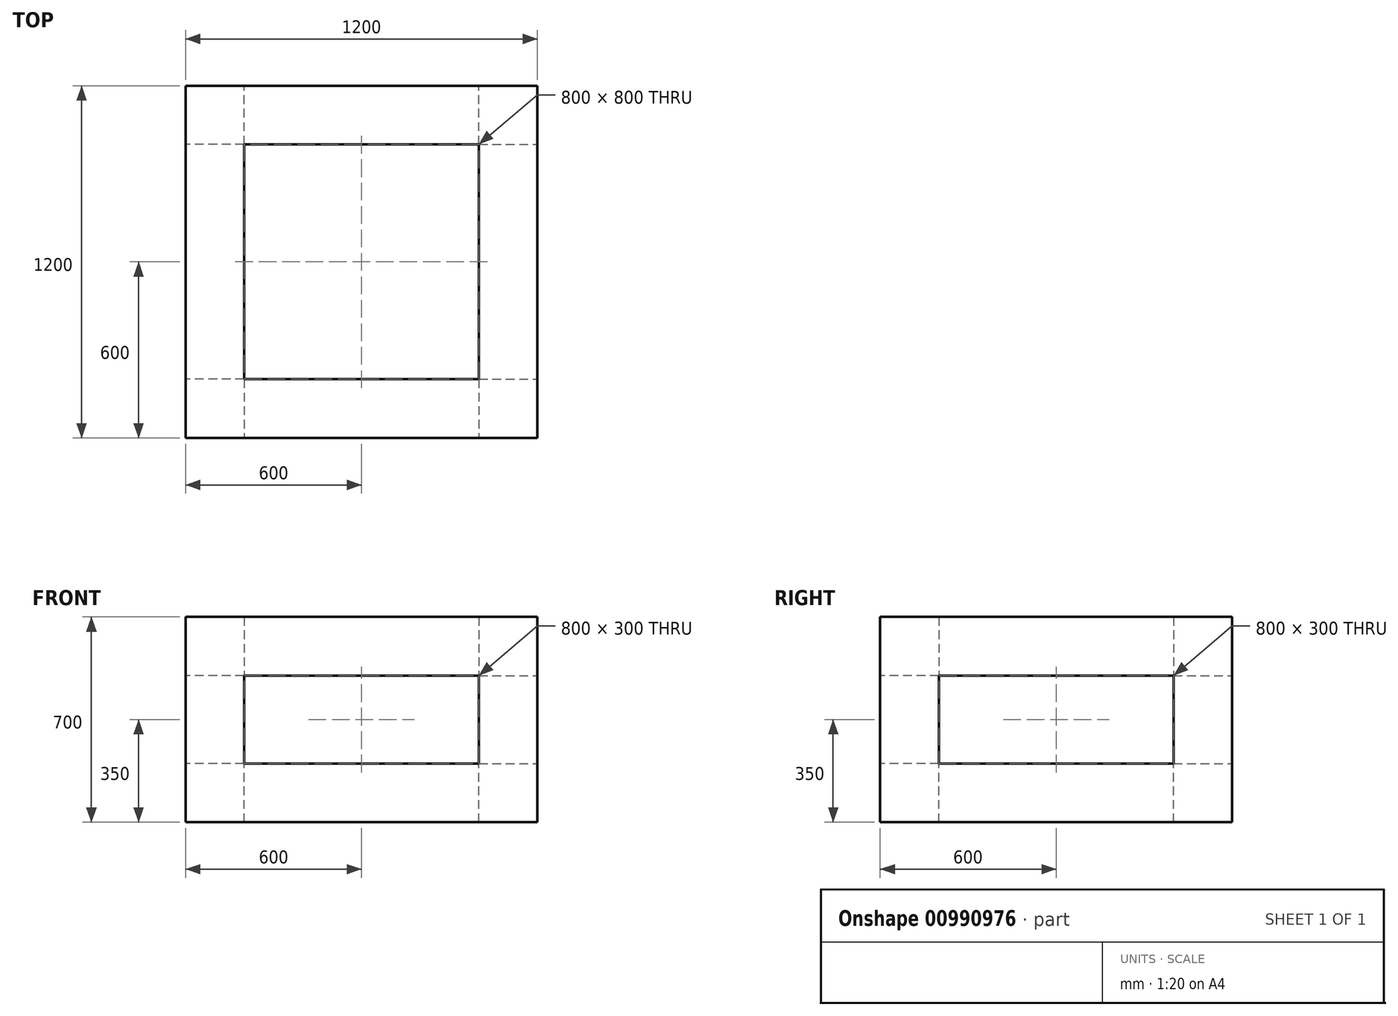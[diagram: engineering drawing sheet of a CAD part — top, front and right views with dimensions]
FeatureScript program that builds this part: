
annotation { "Feature Type Name" : "Feature", "Feature Type Description" : "" }
export const myFeature = defineFeature(function(context is Context, id is Id, definition is map)
    precondition{}
    {
        {
            var Q0;
            Q0=qCreatedBy(makeId("Top.planeOp"),FACE);
            var sketch = newSketch(context, id + "F0", { "sketchPlane" : qUnion([Q0])});
            skLineSegment(sketch, "E0.bottom", {"start": v(600, -600) * mm, "end": v(-600, -600) * mm});
            skLineSegment(sketch, "E0.top", {"start": v(600, 600) * mm, "end": v(-600, 600) * mm});
            skLineSegment(sketch, "E0.left", {"start": v(600, -600) * mm, "end": v(600, 600) * mm});
            skLineSegment(sketch, "E0.right", {"start": v(-600, -600) * mm, "end": v(-600, 600) * mm});
            skPoint(sketch, "E0.middle", {"position": v(0, 0) * mm});
            skLineSegment(sketch, "E1.bottom", {"start": v(400, -400) * mm, "end": v(-400, -400) * mm});
            skLineSegment(sketch, "E1.top", {"start": v(400, 400) * mm, "end": v(-400, 400) * mm});
            skLineSegment(sketch, "E1.left", {"start": v(400, -400) * mm, "end": v(400, 400) * mm});
            skLineSegment(sketch, "E1.right", {"start": v(-400, -400) * mm, "end": v(-400, 400) * mm});
            skLineSegment(sketch, "E2", {"start": v(-400, 400) * mm, "end": v(-600, 400) * mm});
            skLineSegment(sketch, "E3", {"start": v(-400, 400) * mm, "end": v(-400, 600) * mm});
            skLineSegment(sketch, "E4", {"start": v(400, 400) * mm, "end": v(400, 600) * mm});
            skLineSegment(sketch, "E5", {"start": v(400, 400) * mm, "end": v(600, 400) * mm});
            skLineSegment(sketch, "E6", {"start": v(-400, -400) * mm, "end": v(-600, -400) * mm});
            skLineSegment(sketch, "E7", {"start": v(-400, -400) * mm, "end": v(-400, -600) * mm});
            skLineSegment(sketch, "E8", {"start": v(400, -400) * mm, "end": v(600, -400) * mm});
            skLineSegment(sketch, "E9", {"start": v(400, -400) * mm, "end": v(400, -600) * mm});
            skSolve(sketch);
        }
        {
            var Q0;
            {var subQ4=sQuery(id+"F0.wireOp",EDGE,"E2");Q0=makeQuery(id+"F0.imprint","IMPRINT",FACE,{"disambiguationData":[TD([[makeQuery(id+"F0.imprint","IMPRINT",EDGE,{"derivedFrom":subQ4}),-1.0]])]});}
            var Q1;
            Q1=makeQuery(id+"F0.imprint","IMPRINT",FACE,{"disambiguationData":[TD([[makeQuery(id+"F0.imprint","IMPRINT",EDGE,{"derivedFrom":sQuery(id+"F0.wireOp",EDGE,"E1.top")}),-1.0]])]});
            var Q2;
            {var subQ3=sQuery(id+"F0.wireOp",EDGE,"E4");Q2=makeQuery(id+"F0.imprint","IMPRINT",FACE,{"disambiguationData":[TD([[makeQuery(id+"F0.imprint","IMPRINT",EDGE,{"derivedFrom":subQ3}),-1.0]])]});}
            var Q3;
            Q3=makeQuery(id+"F0.imprint","IMPRINT",FACE,{"disambiguationData":[TD([[makeQuery(id+"F0.imprint","IMPRINT",EDGE,{"derivedFrom":sQuery(id+"F0.wireOp",EDGE,"E1.left")}),-1.0]])]});
            var Q4;
            Q4=makeQuery(id+"F0.imprint","IMPRINT",FACE,{"disambiguationData":[TD([[makeQuery(id+"F0.imprint","IMPRINT",EDGE,{"derivedFrom":sQuery(id+"F0.wireOp",EDGE,"E1.bottom")}),-1.0]])]});
            var Q5;
            Q5=makeQuery(id+"F0.imprint","IMPRINT",FACE,{"disambiguationData":[TD([[makeQuery(id+"F0.imprint","IMPRINT",EDGE,{"derivedFrom":sQuery(id+"F0.wireOp",EDGE,"E1.right")}),1.0]])]});
            var Q6;
            {var subQ4=sQuery(id+"F0.wireOp",EDGE,"E6");Q6=makeQuery(id+"F0.imprint","IMPRINT",FACE,{"disambiguationData":[TD([[makeQuery(id+"F0.imprint","IMPRINT",EDGE,{"derivedFrom":subQ4}),1.0]])]});}
            var Q7;
            Q7=makeQuery(id+"F0.imprint","IMPRINT",FACE,{"disambiguationData":[TD([[makeQuery(id+"F0.imprint","IMPRINT",EDGE,{"derivedFrom":sQuery(id+"F0.wireOp",EDGE,"E1.bottom")}),1.0]])]});
            var Q8;
            {var subQ4=sQuery(id+"F0.wireOp",EDGE,"E8");Q8=makeQuery(id+"F0.imprint","IMPRINT",FACE,{"disambiguationData":[TD([[makeQuery(id+"F0.imprint","IMPRINT",EDGE,{"derivedFrom":subQ4}),-1.0]])]});}
            extrude(context, id + "F1", {"entities" : qUnion([Q0, Q1, Q2, Q3, Q4, Q5, Q6, Q7, Q8]), "oppositeDirection" : true, "depth" : 200 * mm, "offsetDistance" : 25 * mm});
        }
        {
            var Q0;
            {var subQ4=sQuery(id+"F0.wireOp",EDGE,"E6");Q0=makeQuery(id+"F0.imprint","IMPRINT",FACE,{"disambiguationData":[TD([[makeQuery(id+"F0.imprint","IMPRINT",EDGE,{"derivedFrom":subQ4}),1.0]])]});}
            var Q1;
            {var subQ4=sQuery(id+"F0.wireOp",EDGE,"E8");Q1=makeQuery(id+"F0.imprint","IMPRINT",FACE,{"disambiguationData":[TD([[makeQuery(id+"F0.imprint","IMPRINT",EDGE,{"derivedFrom":subQ4}),-1.0]])]});}
            var Q2;
            {var subQ3=sQuery(id+"F0.wireOp",EDGE,"E4");Q2=makeQuery(id+"F0.imprint","IMPRINT",FACE,{"disambiguationData":[TD([[makeQuery(id+"F0.imprint","IMPRINT",EDGE,{"derivedFrom":subQ3}),-1.0]])]});}
            var Q3;
            {var subQ4=sQuery(id+"F0.wireOp",EDGE,"E2");Q3=makeQuery(id+"F0.imprint","IMPRINT",FACE,{"disambiguationData":[TD([[makeQuery(id+"F0.imprint","IMPRINT",EDGE,{"derivedFrom":subQ4}),-1.0]])]});}
            extrude(context, id + "F2", {"entities" : qUnion([Q0, Q1, Q2, Q3]), "operationType" : NewBodyOperationType.ADD, "depth" : 300 * mm, "offsetDistance" : 25 * mm});
        }
        {
            var Q0;
            Q0=makeQuery(id+"F0.imprint","IMPRINT",FACE,{"disambiguationData":[TD([[makeQuery(id+"F0.imprint","IMPRINT",EDGE,{"derivedFrom":sQuery(id+"F0.wireOp",EDGE,"E1.bottom")}),-1.0]])]});
            extrude(context, id + "F3", {"entities" : qUnion([Q0]), "operationType" : NewBodyOperationType.REMOVE, "endBound" : BoundingType.THROUGH_ALL, "oppositeDirection" : true, "depth" : 200 * mm, "offsetDistance" : 25 * mm});
        }
        {
            var Q0;
            Q0=makeQuery(id+"F2.opExtrude","CAP_FACE",FACE,{"disambiguationData":[OSD([sQuery(id+"F0.wireOp",EDGE,"E0.bottom"),sQuery(id+"F0.wireOp",EDGE,"E0.left"),sQuery(id+"F0.wireOp",EDGE,"E8"),sQuery(id+"F0.wireOp",EDGE,"E9")])],"isStart":false});
            var sketch = newSketch(context, id + "F4", { "sketchPlane" : qUnion([Q0])});
            skLineSegment(sketch, "E10.bottom", {"start": v(600, -600) * mm, "end": v(-600, -600) * mm});
            skLineSegment(sketch, "E10.top", {"start": v(600, 600) * mm, "end": v(-600, 600) * mm});
            skLineSegment(sketch, "E10.left", {"start": v(600, -600) * mm, "end": v(600, 600) * mm});
            skLineSegment(sketch, "E10.right", {"start": v(-600, -600) * mm, "end": v(-600, 600) * mm});
            skLineSegment(sketch, "E11.bottom", {"start": v(400, -400) * mm, "end": v(-400, -400) * mm});
            skLineSegment(sketch, "E11.top", {"start": v(400, 400) * mm, "end": v(-400, 400) * mm});
            skLineSegment(sketch, "E11.left", {"start": v(400, -400) * mm, "end": v(400, 400) * mm});
            skLineSegment(sketch, "E11.right", {"start": v(-400, -400) * mm, "end": v(-400, 400) * mm});
            skSolve(sketch);
        }
        {
            var Q0;
            {var subQ3=sQuery(id+"F4.wireOp",EDGE,"E10.top");Q0=makeQuery(id+"F4.imprint","IMPRINT",FACE,{"disambiguationData":[TD([[makeQuery(id+"F4.imprint","IMPRINT",EDGE,{"derivedFrom":subQ3}),1.0]])]});}
            var Q1;
            {var subQ4=makeQuery(id+"F2.opExtrude","CAP_EDGE",EDGE,{"disambiguationData":[OSD([sQuery(id+"F0.wireOp",EDGE,"E8")])],"isStart":false});Q1=makeQuery(id+"F4.imprint","IMPRINT",FACE,{"disambiguationData":[TD([[makeQuery(id+"F4.imprint","IMPRINT",EDGE,{"derivedFrom":subQ4}),-1.0]])]});}
            extrude(context, id + "F5", {"entities" : qUnion([Q0, Q1]), "operationType" : NewBodyOperationType.ADD, "depth" : 200 * mm, "offsetDistance" : 25 * mm});
        }
    });
